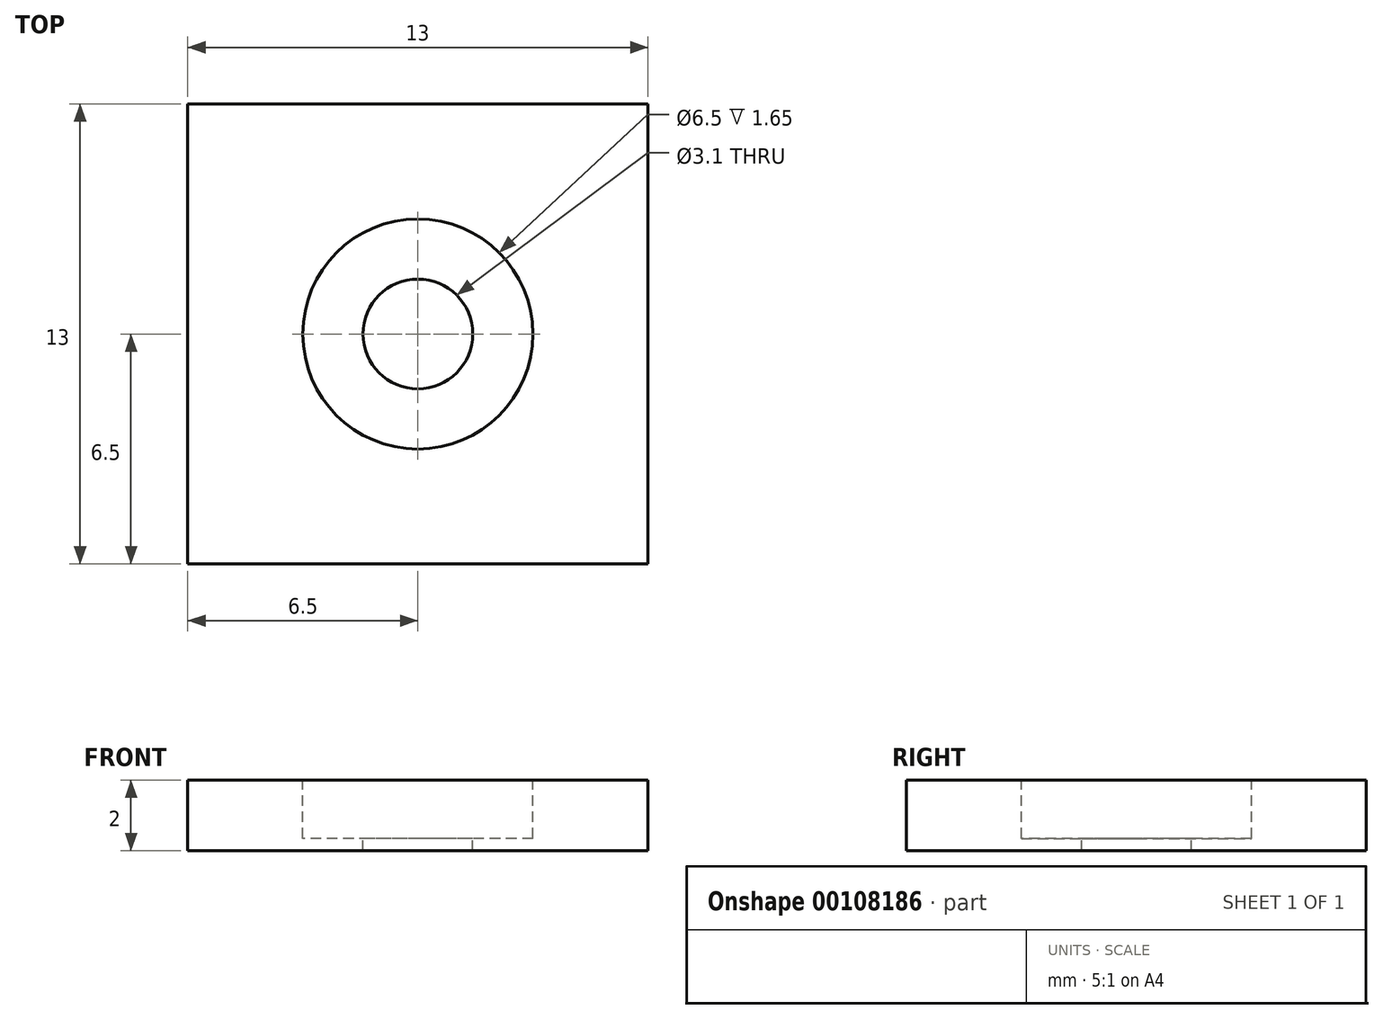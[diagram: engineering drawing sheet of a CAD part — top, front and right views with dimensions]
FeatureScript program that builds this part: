
annotation { "Feature Type Name" : "Feature", "Feature Type Description" : "" }
export const myFeature = defineFeature(function(context is Context, id is Id, definition is map)
    precondition{}
    {
        {
            var Q0;
            Q0=qCreatedBy(makeId("Top.planeOp"),FACE);
            var sketch = newSketch(context, id + "F0", { "sketchPlane" : qUnion([Q0])});
            skLineSegment(sketch, "E0.bottom", {"start": v(-6.5, 6.5) * mm, "end": v(6.5, 6.5) * mm});
            skLineSegment(sketch, "E0.top", {"start": v(-6.5, -6.5) * mm, "end": v(6.5, -6.5) * mm});
            skLineSegment(sketch, "E0.left", {"start": v(-6.5, 6.5) * mm, "end": v(-6.5, -6.5) * mm});
            skLineSegment(sketch, "E0.right", {"start": v(6.5, 6.5) * mm, "end": v(6.5, -6.5) * mm});
            skPoint(sketch, "E0.middle", {"position": v(0, 0) * mm});
            skSolve(sketch);
        }
        {
            var Q0;
            Q0 = qSketchRegion(id + "F0", true);
            extrude(context, id + "F1", {"entities" : qUnion([Q0]), "depth" : 2 * mm});
        }
        {
            var Q0;
            Q0=makeQuery(id+"F1.opExtrude","CAP_FACE",FACE,{"disambiguationData":[OSD([sQuery(id+"F0.wireOp",EDGE,"E0.bottom"),sQuery(id+"F0.wireOp",EDGE,"E0.top"),sQuery(id+"F0.wireOp",EDGE,"E0.left"),sQuery(id+"F0.wireOp",EDGE,"E0.right")])],"isStart":false});
            var sketch = newSketch(context, id + "F2", { "sketchPlane" : qUnion([Q0])});
            skCircle(sketch, "E1", {"center": v(0, 0) * mm, "radius": 3.25 * mm});
            skSolve(sketch);
        }
        {
            var Q0;
            Q0 = qSketchRegion(id + "F2", true);
            extrude(context, id + "F3", {"entities" : qUnion([Q0]), "operationType" : NewBodyOperationType.REMOVE, "oppositeDirection" : true, "depth" : 1.65 * mm});
        }
        {
            var Q0;
            Q0=makeQuery(id+"F3.boolean.opBoolean","COPY",FACE,{"derivedFrom":makeQuery(id+"F3.opExtrude","CAP_FACE",FACE,{"disambiguationData":[OSD([sQuery(id+"F2.wireOp",EDGE,"E1")])],"isStart":false})});
            var sketch = newSketch(context, id + "F4", { "sketchPlane" : qUnion([Q0])});
            skCircle(sketch, "E2", {"center": v(0, 0) * mm, "radius": 1.55 * mm});
            skSolve(sketch);
        }
        {
            var Q0;
            Q0 = qSketchRegion(id + "F4", true);
            extrude(context, id + "F5", {"entities" : qUnion([Q0]), "operationType" : NewBodyOperationType.REMOVE, "oppositeDirection" : true, "depth" : 1 * mm});
        }
    });
